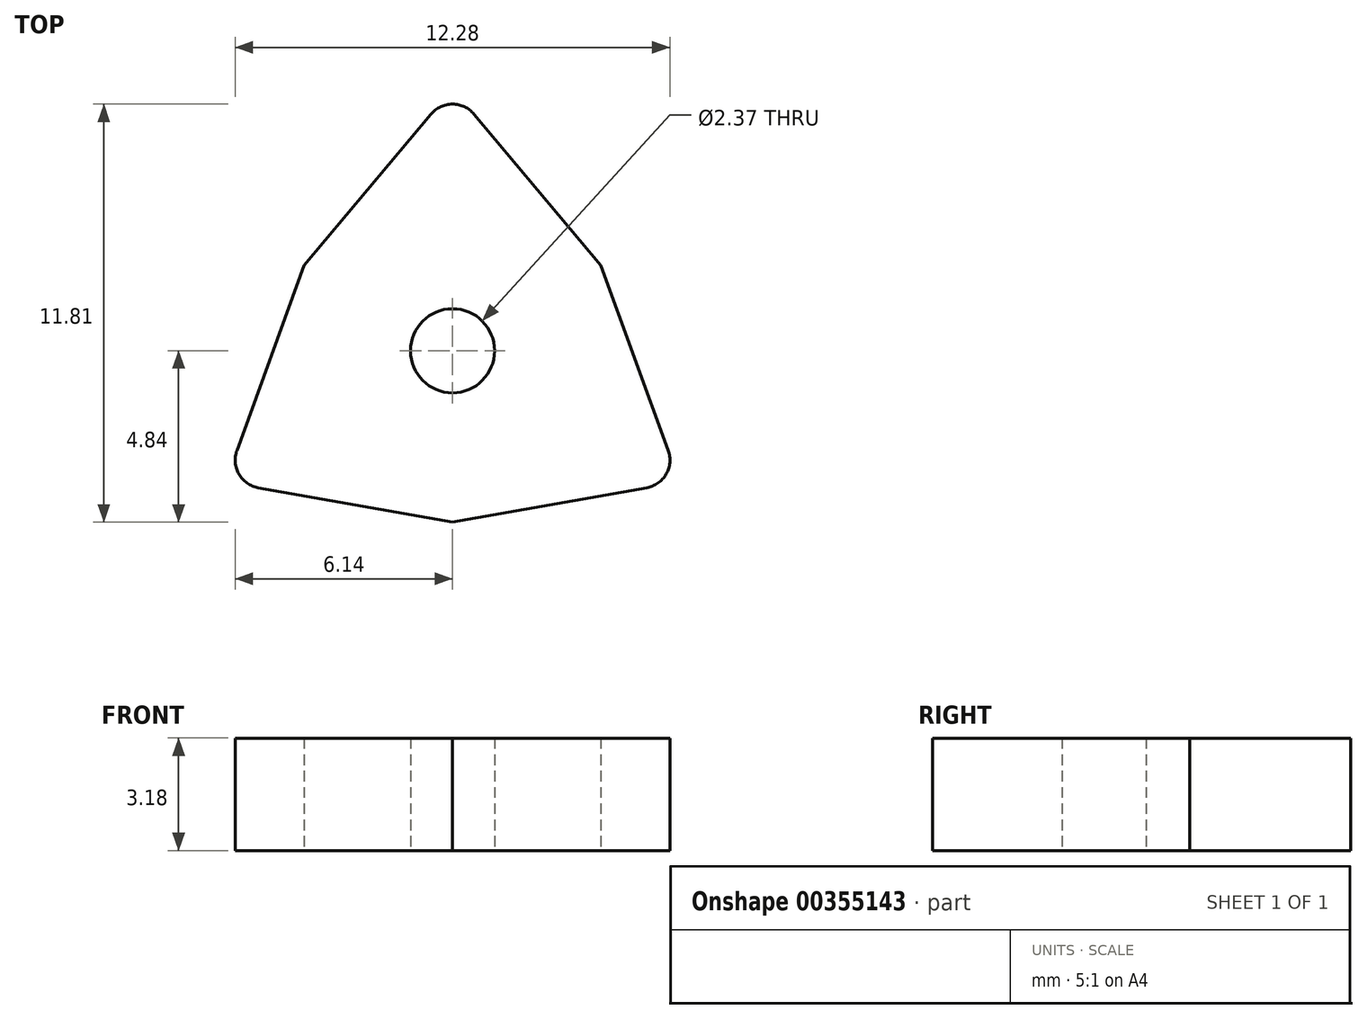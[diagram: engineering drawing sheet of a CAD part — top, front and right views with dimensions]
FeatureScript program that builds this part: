
annotation { "Feature Type Name" : "Feature", "Feature Type Description" : "" }
export const myFeature = defineFeature(function(context is Context, id is Id, definition is map)
    precondition{}
    {
        {
            var Q0;
            Q0=qCreatedBy(makeId("Top.planeOp"),FACE);
            var sketch = newSketch(context, id + "F0", { "sketchPlane" : qUnion([Q0])});
            skCircle(sketch, "E0", {"center": v(0, 0) * mm, "radius": 4.76 * mm});
            skLineSegment(sketch, "E1", {"start": v(0, 0) * mm, "end": v(0, 7.4) * mm});
            skLineSegment(sketch, "E2", {"start": v(0, 7.4) * mm, "end": v(5.64, 0.7) * mm});
            skLineSegment(sketch, "E3.MirrorCS", {"start": v(0, 7.4) * mm, "end": v(-4.19, 2.42) * mm});
            skLineSegment(sketch, "E4.MirrorCS", {"start": v(0, 7.4) * mm, "end": v(4.19, 2.42) * mm});
            skLineSegment(sketch, "E5.1.0", {"start": v(-6.42, -3.7) * mm, "end": v(-4.19, 2.42) * mm});
            skLineSegment(sketch, "E5.1.1", {"start": v(-6.42, -3.7) * mm, "end": v(0, -4.84) * mm});
            skLineSegment(sketch, "E5.2.0", {"start": v(6.42, -3.7) * mm, "end": v(0, -4.84) * mm});
            skLineSegment(sketch, "E5.2.1", {"start": v(6.42, -3.7) * mm, "end": v(4.19, 2.42) * mm});
            skPoint(sketch, "E6.orphan", {"position": v(-3.42, 4.54) * mm});
            skPoint(sketch, "E7.orphan", {"position": v(-5.64, 0.7) * mm});
            skPoint(sketch, "E8.orphan", {"position": v(3.42, 4.54) * mm});
            skPoint(sketch, "E9.orphan", {"position": v(5.64, 0.7) * mm});
            skPoint(sketch, "E10.orphan", {"position": v(2.22, -5.23) * mm});
            skPoint(sketch, "E11.orphan", {"position": v(-2.22, -5.23) * mm});
            skCircle(sketch, "E12", {"center": v(0, 0) * mm, "radius": 1.19 * mm});
            skSolve(sketch);
        }
        {
            var Q0;
            {var subQ0=sQuery(id+"F0.wireOp",EDGE,"E4.MirrorCS");var subQ1=sQuery(id+"F0.wireOp",EDGE,"E0");var subQ2=makeQuery(id+"F0.imprint","INTERSECT",VERTEX,{"derivedFrom":[subQ1,subQ0]});Q0=makeQuery(id+"F0.imprint","IMPRINT",FACE,{"disambiguationData":[TD([[makeQuery(id+"F0.imprint","IMPRINT",EDGE,{"disambiguationData":[TD([[subQ2,-1.0]])],"derivedFrom":subQ1}),-1.0]])]});}
            var Q1;
            {var subQ0=sQuery(id+"F0.wireOp",EDGE,"E1");var subQ1=sQuery(id+"F0.wireOp",EDGE,"E0");var subQ2=makeQuery(id+"F0.imprint","INTERSECT",VERTEX,{"derivedFrom":[subQ1,subQ0]});Q1=makeQuery(id+"F0.imprint","IMPRINT",FACE,{"disambiguationData":[TD([[makeQuery(id+"F0.imprint","IMPRINT",EDGE,{"disambiguationData":[TD([[subQ2,-1.0]])],"derivedFrom":subQ1}),-1.0]])]});}
            var Q2;
            Q2=makeQuery(id+"F0.imprint","IMPRINT",FACE,{"disambiguationData":[TD([[makeQuery(id+"F0.imprint","IMPRINT",EDGE,{"derivedFrom":sQuery(id+"F0.wireOp",EDGE,"E12")}),-1.0]])]});
            var Q3;
            {var subQ0=sQuery(id+"F0.wireOp",EDGE,"E5.2.1");var subQ1=sQuery(id+"F0.wireOp",EDGE,"E0");var subQ2=makeQuery(id+"F0.imprint","INTERSECT",VERTEX,{"derivedFrom":[subQ1,subQ0]});Q3=makeQuery(id+"F0.imprint","IMPRINT",FACE,{"disambiguationData":[TD([[makeQuery(id+"F0.imprint","IMPRINT",EDGE,{"disambiguationData":[TD([[subQ2,1.0]])],"derivedFrom":subQ1}),-1.0]])]});}
            var Q4;
            {var subQ0=sQuery(id+"F0.wireOp",EDGE,"E5.1.0");var subQ1=sQuery(id+"F0.wireOp",EDGE,"E0");var subQ2=makeQuery(id+"F0.imprint","INTERSECT",VERTEX,{"derivedFrom":[subQ1,subQ0]});Q4=makeQuery(id+"F0.imprint","IMPRINT",FACE,{"disambiguationData":[TD([[makeQuery(id+"F0.imprint","IMPRINT",EDGE,{"disambiguationData":[TD([[subQ2,-1.0]])],"derivedFrom":subQ1}),-1.0]])]});}
            var Q5;
            {var subQ0=sQuery(id+"F0.wireOp",EDGE,"E4.MirrorCS");var subQ1=sQuery(id+"F0.wireOp",EDGE,"E0");var subQ2=makeQuery(id+"F0.imprint","INTERSECT",VERTEX,{"derivedFrom":[subQ1,subQ0]});Q5=makeQuery(id+"F0.imprint","IMPRINT",FACE,{"disambiguationData":[TD([[makeQuery(id+"F0.imprint","IMPRINT",EDGE,{"disambiguationData":[TD([[subQ2,1.0]])],"derivedFrom":subQ1}),-1.0]])]});}
            var Q6;
            {var subQ0=sQuery(id+"F0.wireOp",EDGE,"E3.MirrorCS");var subQ1=sQuery(id+"F0.wireOp",EDGE,"E0");var subQ2=makeQuery(id+"F0.imprint","INTERSECT",VERTEX,{"derivedFrom":[subQ1,subQ0]});Q6=makeQuery(id+"F0.imprint","IMPRINT",FACE,{"disambiguationData":[TD([[makeQuery(id+"F0.imprint","IMPRINT",EDGE,{"disambiguationData":[TD([[subQ2,-1.0]])],"derivedFrom":subQ1}),-1.0]])]});}
            var Q7;
            {var subQ0=sQuery(id+"F0.wireOp",EDGE,"E5.1.1");var subQ1=sQuery(id+"F0.wireOp",EDGE,"E0");var subQ2=makeQuery(id+"F0.imprint","INTERSECT",VERTEX,{"derivedFrom":[subQ1,subQ0]});Q7=makeQuery(id+"F0.imprint","IMPRINT",FACE,{"disambiguationData":[TD([[makeQuery(id+"F0.imprint","IMPRINT",EDGE,{"disambiguationData":[TD([[subQ2,-1.0]])],"derivedFrom":subQ1}),-1.0]])]});}
            extrude(context, id + "F1", {"entities" : qUnion([Q0, Q1, Q2, Q3, Q4, Q5, Q6, Q7]), "depth" : 3.17 * mm});
        }
        {
            var Q0;
            Q0=makeQuery(id+"F1.opExtrude","SWEPT_EDGE",EDGE,{"disambiguationData":[OSD([sQuery(id+"F0.wireOp",EDGE,"E1"),sQuery(id+"F0.wireOp",EDGE,"E3.MirrorCS"),sQuery(id+"F0.wireOp",EDGE,"E4.MirrorCS")])]});
            var Q1;
            Q1=makeQuery(id+"F1.opExtrude","SWEPT_EDGE",EDGE,{"disambiguationData":[OSD([sQuery(id+"F0.wireOp",EDGE,"E5.1.0"),sQuery(id+"F0.wireOp",EDGE,"E5.1.1")])]});
            var Q2;
            Q2=makeQuery(id+"F1.opExtrude","SWEPT_EDGE",EDGE,{"disambiguationData":[OSD([sQuery(id+"F0.wireOp",EDGE,"E5.2.0"),sQuery(id+"F0.wireOp",EDGE,"E5.2.1")])]});
            fillet(context, id + "F2", {"entities" : qUnion([Q0, Q1, Q2]), "radius" : 0.8 * mm, "tangentPropagation" : true, "allowEdgeOverflow" : false});
        }
    });
